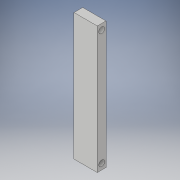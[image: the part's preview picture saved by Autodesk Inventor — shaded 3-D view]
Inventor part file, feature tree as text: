
AUTODESK INVENTOR PART (.ipt)
format: ipt  version: 2017 (Build 210142000, 142)  size: 99,328 bytes
history: native  units: in
note: dims shown in document units (in); Inventor stores cm internally (conversion verified against a paired STEP export)
features: extrude x1, sketch x1
ambient origin geometry x8: Origin, YZ Plane, XZ Plane, XY Plane, X Axis, Y Axis, Z Axis, Center Point
bodies: Solid1 (feature_tree)
feature tree (2):
  extrude  "Extrusion1"  Depth=0.75in
  sketch  "Sketch1"  dims[d0=10.89in d1=0.75in d2=0.5in d3=0.5in d4=0.5in d5=0.5in d6=2.0in d7=0.0in]
